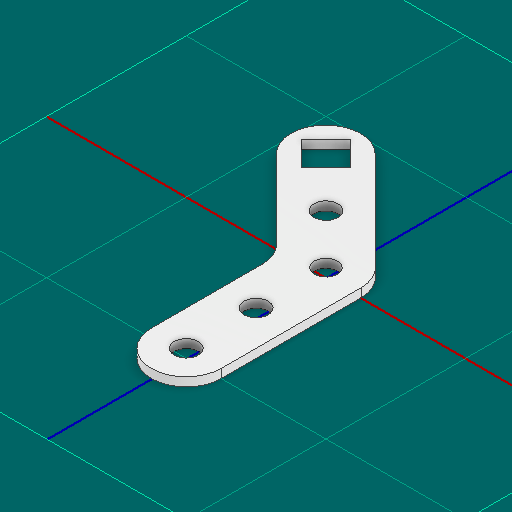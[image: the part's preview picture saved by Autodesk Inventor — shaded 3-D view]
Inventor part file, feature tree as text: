
AUTODESK INVENTOR PART (.ipt)
format: ipt  version: 2025 (Build 290162000, 162)  size: 140,288 bytes
history: native  units: in
note: dims shown in document units (in); Inventor stores cm internally (conversion verified against a paired STEP export)
features: other x5, sketch x1
ambient origin geometry x8: Origin, YZ Plane, XZ Plane, XY Plane, X Axis, Y Axis, Z Axis, Center Point
bodies: Solid1 (feature_tree)
feature tree (6):
  other  "gusset.ipt"
  other  "Blocks"
  other  "main"
  other  "Solid1::gusset.ipt"
  other  "TaggingFeature1"
  sketch  "Sketch1"  dims[d0=0.3937in d5=0.5in d6=0.25in d9=0.248in d10=45.0deg d11=0.248in]
